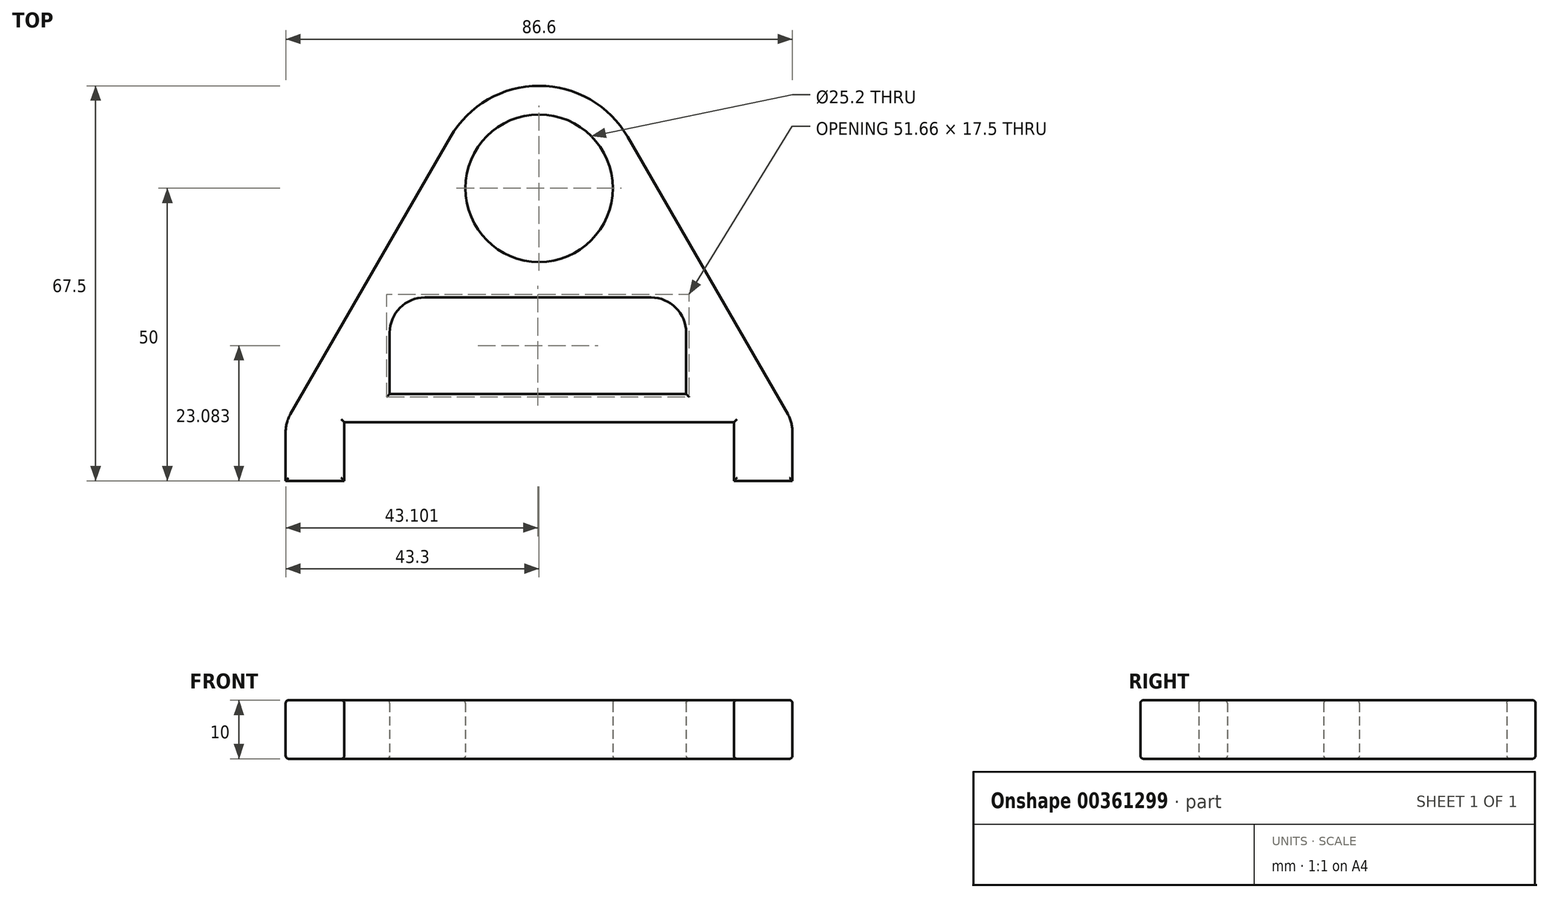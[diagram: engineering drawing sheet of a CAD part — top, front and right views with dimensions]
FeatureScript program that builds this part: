
annotation { "Feature Type Name" : "Feature", "Feature Type Description" : "" }
export const myFeature = defineFeature(function(context is Context, id is Id, definition is map)
    precondition{}
    {
        {
            var Q0;
            Q0=qCreatedBy(makeId("Top.planeOp"),FACE);
            var sketch = newSketch(context, id + "F0", { "sketchPlane" : qUnion([Q0])});
            skCircle(sketch, "E0", {"center": v(0, 0) * mm, "radius": 40 * mm, "construction": true});
            skCircle(sketch, "E1", {"center": v(0, 0) * mm, "radius": 12.6 * mm});
            skArc(sketch, "E2", {"start": v(15.16, 8.75) * mm, "mid": v(0, 17.5) * mm, "end": v(-15.16, 8.75) * mm});
            skLineSegment(sketch, "E3", {"start": v(-33.3, -40) * mm, "end": v(33.3, -40) * mm});
            skLineSegment(sketch, "E4.trimOffspring", {"start": v(-15.16, 8.75) * mm, "end": v(-42.5, -38.6) * mm});
            skLineSegment(sketch, "E5", {"start": v(15.16, 8.75) * mm, "end": v(42.5, -38.6) * mm});
            skLineSegment(sketch, "E6.top", {"start": v(-43.3, -50) * mm, "end": v(-33.3, -50) * mm});
            skLineSegment(sketch, "E6.left", {"start": v(-43.3, -41.6) * mm, "end": v(-43.3, -50) * mm});
            skLineSegment(sketch, "E6.right", {"start": v(-33.3, -40) * mm, "end": v(-33.3, -50) * mm});
            skLineSegment(sketch, "E7.top", {"start": v(43.3, -50) * mm, "end": v(33.3, -50) * mm});
            skLineSegment(sketch, "E7.left", {"start": v(43.3, -41.6) * mm, "end": v(43.3, -50) * mm});
            skLineSegment(sketch, "E7.right", {"start": v(33.3, -40) * mm, "end": v(33.3, -50) * mm});
            skLineSegment(sketch, "E8.bottom", {"start": v(19.13, -18.67) * mm, "end": v(-19.53, -18.67) * mm});
            skLineSegment(sketch, "E8.top", {"start": v(25.13, -35.17) * mm, "end": v(-25.53, -35.17) * mm});
            skLineSegment(sketch, "E8.left", {"start": v(25.13, -24.67) * mm, "end": v(25.13, -35.17) * mm});
            skLineSegment(sketch, "E8.right", {"start": v(-25.53, -24.67) * mm, "end": v(-25.53, -35.17) * mm});
            skPoint(sketch, "E9.visualSharp", {"position": v(-25.53, -18.67) * mm});
            skArc(sketch, "E9.filletArc", {"start": v(-19.53, -18.67) * mm, "mid": v(-23.77, -20.43) * mm, "end": v(-25.53, -24.67) * mm});
            skPoint(sketch, "E10.visualSharp", {"position": v(25.13, -18.67) * mm});
            skArc(sketch, "E10.filletArc", {"start": v(25.13, -24.67) * mm, "mid": v(23.38, -20.43) * mm, "end": v(19.13, -18.67) * mm});
            skPoint(sketch, "E11.visualSharp", {"position": v(-43.3, -40) * mm});
            skArc(sketch, "E11.filletArc", {"start": v(-42.5, -38.6) * mm, "mid": v(-43.1, -40.05) * mm, "end": v(-43.3, -41.6) * mm});
            skPoint(sketch, "E12.visualSharp", {"position": v(43.3, -40) * mm});
            skArc(sketch, "E12.filletArc", {"start": v(43.3, -41.6) * mm, "mid": v(43.1, -40.05) * mm, "end": v(42.5, -38.6) * mm});
            skSolve(sketch);
        }
        {
            var Q0;
            Q0=makeQuery(id+"F0.imprint","IMPRINT",FACE,{"disambiguationData":[TD([[makeQuery(id+"F0.imprint","IMPRINT",EDGE,{"derivedFrom":sQuery(id+"F0.wireOp",EDGE,"E1")}),-1.0]])]});
            extrude(context, id + "F1", {"entities" : qUnion([Q0]), "depth" : 10 * mm});
        }
        {
            var Q0;
            Q0=makeQuery(id+"F1.opExtrude","CAP_FACE",FACE,{"disambiguationData":[OSD([sQuery(id+"F0.wireOp",EDGE,"E1"),sQuery(id+"F0.wireOp",EDGE,"E2"),sQuery(id+"F0.wireOp",EDGE,"E3"),sQuery(id+"F0.wireOp",EDGE,"E4.trimOffspring"),sQuery(id+"F0.wireOp",EDGE,"E5"),sQuery(id+"F0.wireOp",EDGE,"E6.top"),sQuery(id+"F0.wireOp",EDGE,"E6.left"),sQuery(id+"F0.wireOp",EDGE,"E6.right"),sQuery(id+"F0.wireOp",EDGE,"E7.top"),sQuery(id+"F0.wireOp",EDGE,"E7.left"),sQuery(id+"F0.wireOp",EDGE,"E7.right"),sQuery(id+"F0.wireOp",EDGE,"E8.bottom"),sQuery(id+"F0.wireOp",EDGE,"E8.top"),sQuery(id+"F0.wireOp",EDGE,"E8.left"),sQuery(id+"F0.wireOp",EDGE,"E8.right"),sQuery(id+"F0.wireOp",EDGE,"E9.filletArc"),sQuery(id+"F0.wireOp",EDGE,"E10.filletArc"),sQuery(id+"F0.wireOp",EDGE,"E11.filletArc"),sQuery(id+"F0.wireOp",EDGE,"E12.filletArc")])],"isStart":false});
            var Q1;
            Q1=makeQuery(id+"F1.opExtrude","CAP_FACE",FACE,{"disambiguationData":[OSD([sQuery(id+"F0.wireOp",EDGE,"E1"),sQuery(id+"F0.wireOp",EDGE,"E2"),sQuery(id+"F0.wireOp",EDGE,"E3"),sQuery(id+"F0.wireOp",EDGE,"E4.trimOffspring"),sQuery(id+"F0.wireOp",EDGE,"E5"),sQuery(id+"F0.wireOp",EDGE,"E6.top"),sQuery(id+"F0.wireOp",EDGE,"E6.left"),sQuery(id+"F0.wireOp",EDGE,"E6.right"),sQuery(id+"F0.wireOp",EDGE,"E7.top"),sQuery(id+"F0.wireOp",EDGE,"E7.left"),sQuery(id+"F0.wireOp",EDGE,"E7.right"),sQuery(id+"F0.wireOp",EDGE,"E8.bottom"),sQuery(id+"F0.wireOp",EDGE,"E8.top"),sQuery(id+"F0.wireOp",EDGE,"E8.left"),sQuery(id+"F0.wireOp",EDGE,"E8.right"),sQuery(id+"F0.wireOp",EDGE,"E9.filletArc"),sQuery(id+"F0.wireOp",EDGE,"E10.filletArc"),sQuery(id+"F0.wireOp",EDGE,"E11.filletArc"),sQuery(id+"F0.wireOp",EDGE,"E12.filletArc")])],"isStart":true});
            fillet(context, id + "F2", {"entities" : qUnion([Q0, Q1]), "radius" : 0.5 * mm, "tangentPropagation" : true, "allowEdgeOverflow" : false});
        }
    });
